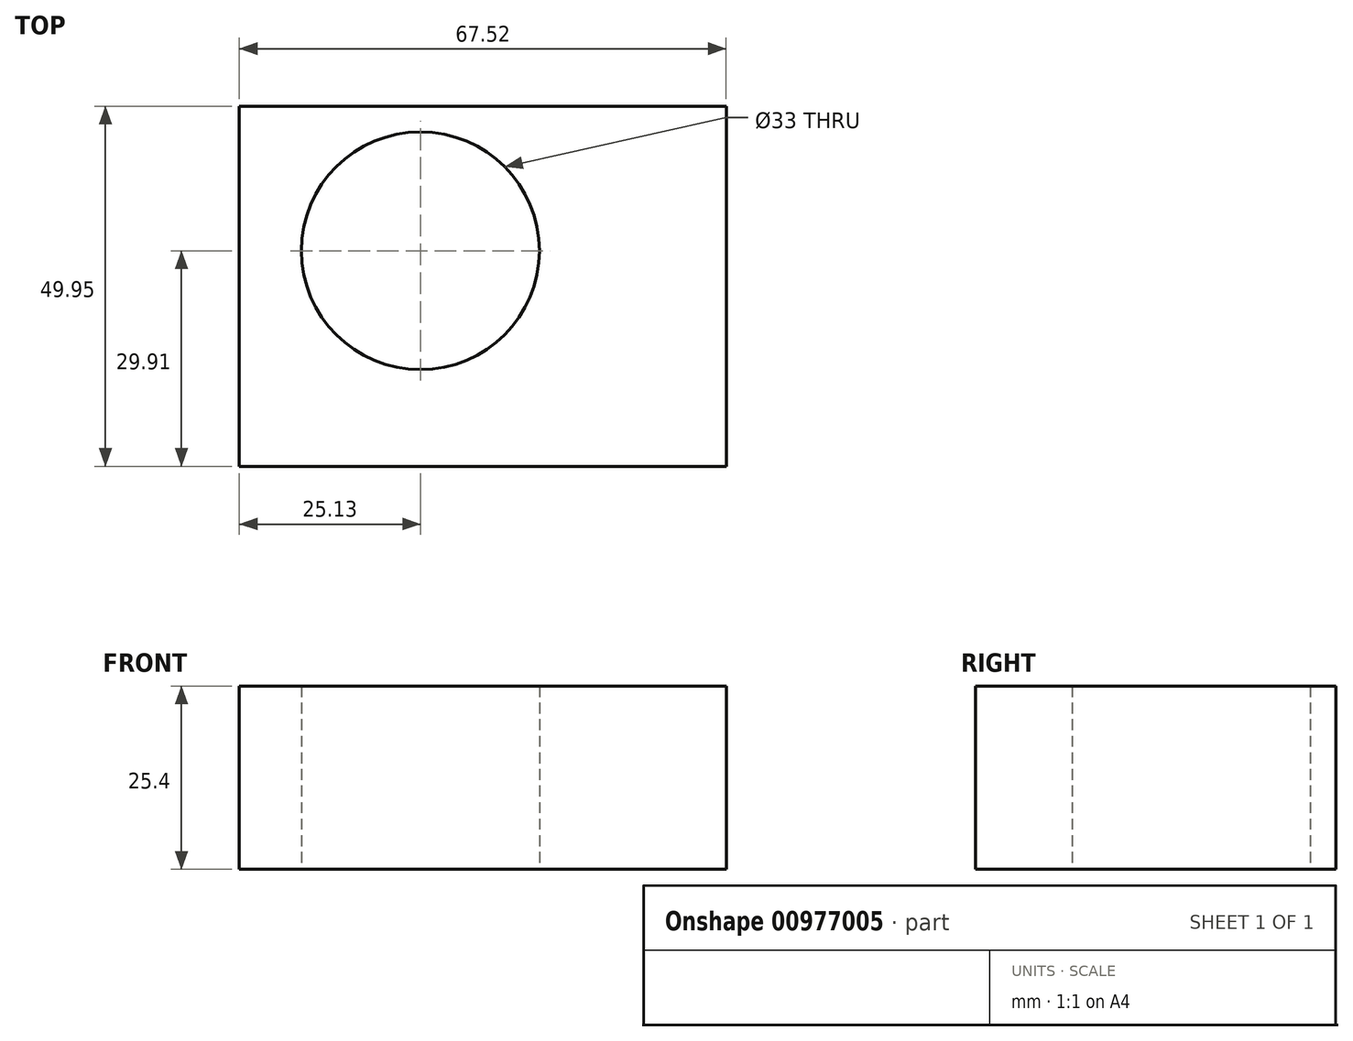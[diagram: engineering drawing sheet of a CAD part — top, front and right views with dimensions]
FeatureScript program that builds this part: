
annotation { "Feature Type Name" : "Feature", "Feature Type Description" : "" }
export const myFeature = defineFeature(function(context is Context, id is Id, definition is map)
    precondition{}
    {
        {
            var Q0;
            Q0=qCreatedBy(makeId("Top.planeOp"),FACE);
            var sketch = newSketch(context, id + "F0", { "sketchPlane" : qUnion([Q0])});
            skLineSegment(sketch, "E0.bottom", {"start": v(-25.13, 20.04) * mm, "end": v(42.4, 20.04) * mm});
            skLineSegment(sketch, "E0.top", {"start": v(-25.13, -29.9) * mm, "end": v(42.4, -29.9) * mm});
            skLineSegment(sketch, "E0.left", {"start": v(-25.13, 20.04) * mm, "end": v(-25.13, -29.9) * mm});
            skLineSegment(sketch, "E0.right", {"start": v(42.4, 20.04) * mm, "end": v(42.4, -29.9) * mm});
            skCircle(sketch, "E1", {"center": v(0, 0) * mm, "radius": 16.5 * mm});
            skSolve(sketch);
        }
        {
            var Q0;
            Q0=makeQuery(id+"F0.imprint","IMPRINT",FACE,{"disambiguationData":[TD([[makeQuery(id+"F0.imprint","IMPRINT",EDGE,{"derivedFrom":sQuery(id+"F0.wireOp",EDGE,"E0.bottom")}),-1.0]])]});
            extrude(context, id + "F1", {"entities" : qUnion([Q0]), "depth" : 25.4 * mm, "offsetDistance" : 25.4 * mm});
        }
    });
